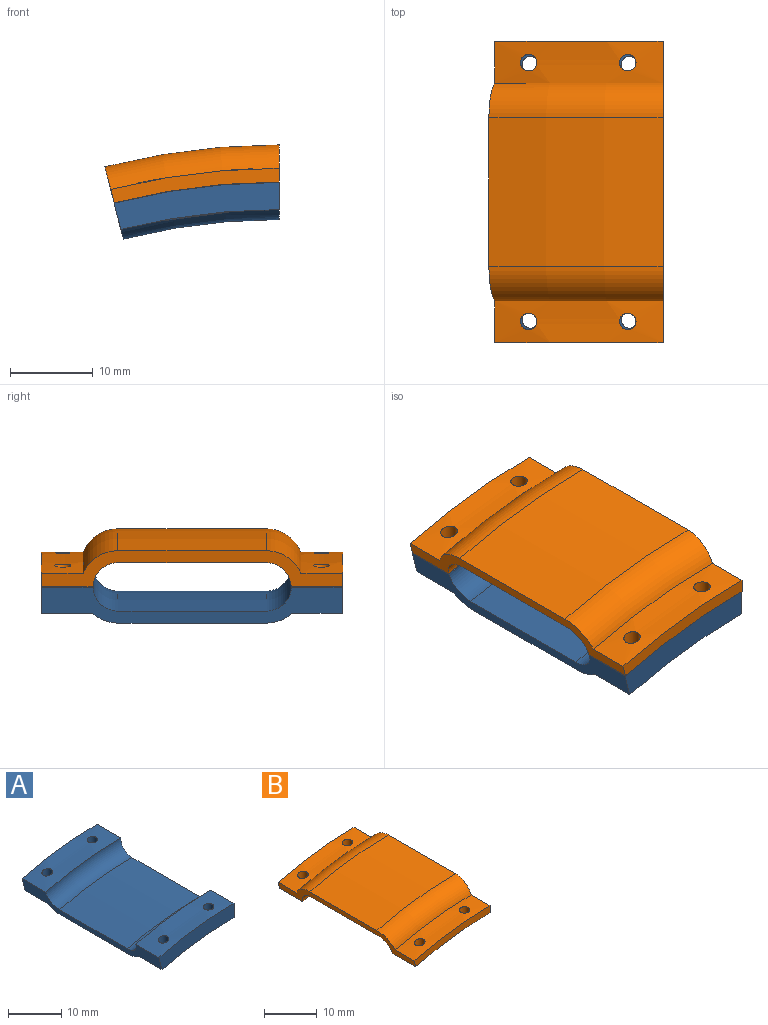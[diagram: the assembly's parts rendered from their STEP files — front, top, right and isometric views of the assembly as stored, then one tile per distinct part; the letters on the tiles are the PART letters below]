
ASSEMBLY  parts=2 mates=1
PART A: 18 faces, bbox 20.7x36.5x9.7 mm
  f0: cylinder r=77.35mm len=19.17mm, axis (0,-1,0), area 111.8mm2, adj f2,f3,f9,f10,f14,f15
  f1: cylinder r=80.65mm len=19.98mm, axis (0,-1,0), area 118.1mm2, adj f2,f3,f10,f11,f14,f15
  f2: plane 36.45x4.5mm, normal (1,0,0), area 78.7mm2, adj f0,f1,f4,f5,f6,f7,f8,f9
  f3: plane 36.45x4.36mm, normal (-0.97,0,-0.25), area 78.7mm2, adj f0,f1,f4,f5,f6,f7,f8,f9
  f4: cylinder r=80.65mm len=19.98mm, axis (0,-1,0), area 120.6mm2, adj f2,f3,f5,f13,f16,f17
  f5: plane 19.98x5.71mm, normal (0,1,0), area 65.1mm2, adj f2,f3,f4,f6
  f6: cylinder r=77.35mm len=19.17mm, axis (0,-1,0), area 114.1mm2, adj f2,f3,f5,f7,f16,f17
  f7: torus R=80.65mm, axis (0,-1,0), area 64.7mm2, adj f2,f3,f6,f8
  f8: cylinder r=76.15mm len=18.87mm, axis (0,-1,0), area 343.2mm2, adj f2,f3,f7,f9
  f9: torus R=80.65mm, axis (0,-1,0), area 64.7mm2, adj f0,f2,f3,f8
  f10: plane 19.98x5.71mm, normal (0,-1,0), area 65.1mm2, adj f0,f1,f2,f3
  f11: torus R=80.65mm, axis (0,-1,0), area 92.9mm2, adj f1,f2,f3,f12
  f12: cylinder r=77.65mm len=19.24mm, axis (0,-1,0), area 349.9mm2, adj f2,f3,f11,f13
  f13: torus R=80.65mm, axis (0,-1,0), area 92.9mm2, adj f2,f3,f4,f12
  f14: cylinder r=1mm len=3.4mm, axis (0,0,1), area 20.7mm2, adj f0,f1
  f15: cylinder r=1mm len=3.78mm, axis (0,0,1), area 21.1mm2, adj f0,f1
  f16: cylinder r=1mm len=3.78mm, axis (0,0,1), area 21.1mm2, adj f4,f6
  f17: cylinder r=1mm len=3.4mm, axis (0,0,1), area 20.7mm2, adj f4,f6
PART B: 18 faces, bbox 21.3x36.5x9.8 mm
  f0: cylinder r=82.31mm len=20.39mm, axis (0,-1,0), area 98mm2, adj f2,f3,f4,f13,f16,f17
  f1: cylinder r=80.65mm len=19.98mm, axis (0,-1,0), area 119.8mm2, adj f2,f3,f4,f5,f16,f17
  f2: plane 36.5x4.5mm, normal (1,0,0), area 60.8mm2, adj f0,f1,f4,f5,f6,f7,f8,f9
  f3: plane 36.5x4.36mm, normal (-0.97,0,-0.25), area 60.8mm2, adj f0,f1,f4,f5,f6,f7,f8,f9
  f4: plane 20.39x4.18mm, normal (0,1,0), area 34mm2, adj f0,f1,f2,f3
  f5: torus R=80.65mm, axis (0,-1,0), area 97.4mm2, adj f1,f2,f3,f6
  f6: cylinder r=83.65mm len=20.73mm, axis (0,-1,0), area 377mm2, adj f2,f3,f5,f7
  f7: torus R=80.65mm, axis (0,-1,0), area 97.4mm2, adj f2,f3,f6,f8
  f8: cylinder r=80.65mm len=19.98mm, axis (0,-1,0), area 119.8mm2, adj f2,f3,f7,f9,f14,f15
  f9: plane 20.39x4.18mm, normal (0,-1,0), area 34mm2, adj f2,f3,f8,f10
  f10: cylinder r=82.31mm len=20.39mm, axis (0,-1,0), area 98mm2, adj f2,f3,f9,f11,f14,f15
  f11: torus R=80.65mm, axis (0,-1,0), area 113mm2, adj f2,f3,f10,f12
  f12: cylinder r=85.15mm len=21.1mm, axis (0,-1,0), area 383.7mm2, adj f2,f3,f11,f13
  f13: torus R=80.65mm, axis (0,-1,0), area 113mm2, adj f0,f2,f3,f12
  f14: cylinder r=1mm len=2mm, axis (0,0,-1), area 10.5mm2, adj f8,f10
  f15: cylinder r=1mm len=2.11mm, axis (0,0,-1), area 10.7mm2, adj f8,f10
  f16: cylinder r=1mm len=2.11mm, axis (0,0,-1), area 10.7mm2, adj f0,f1
  f17: cylinder r=1mm len=2mm, axis (0,0,-1), area 10.5mm2, adj f0,f1
PLACE A t=(8.8,2.3,-1.14)mm
PLACE B t=(8.8,2.32,-1.1)mm
MATE planar B.f2 <-> A.f2  axis (1,0,0) through (8.8,-12.8,0.4)mm
